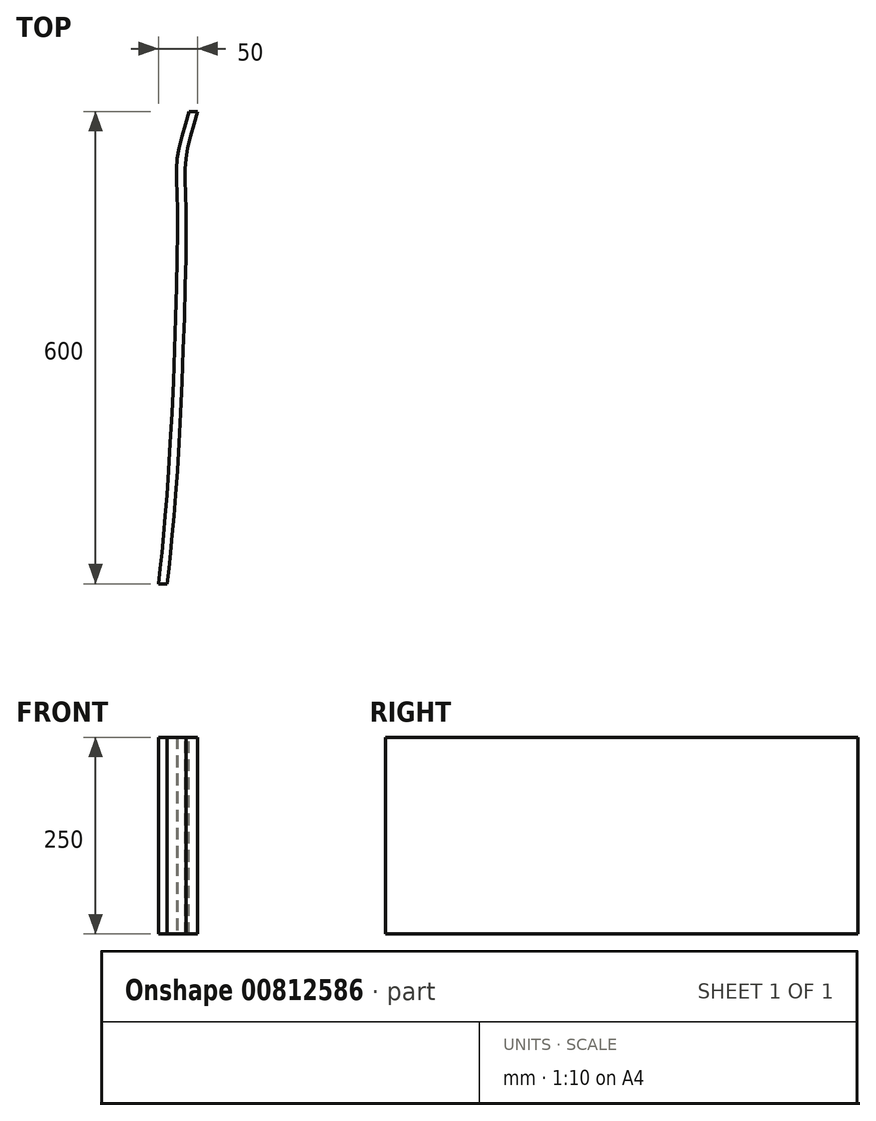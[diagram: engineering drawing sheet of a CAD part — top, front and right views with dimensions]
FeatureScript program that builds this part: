
annotation { "Feature Type Name" : "Feature", "Feature Type Description" : "" }
export const myFeature = defineFeature(function(context is Context, id is Id, definition is map)
    precondition{}
    {
        {
            var Q0;
            Q0=qCreatedBy(makeId("Front.planeOp"),FACE);
            var sketch = newSketch(context, id + "F0", { "sketchPlane" : qUnion([Q0])});
            skLineSegment(sketch, "E0", {"start": v(0, 0) * mm, "end": v(-800, 0) * mm});
            skLineSegment(sketch, "E1", {"start": v(0, 0) * mm, "end": v(800, 0) * mm});
            skPoint(sketch, "E2", {"position": v(800, 0) * mm});
            skSolve(sketch);
        }
        {
            var Q0;
            Q0=qCreatedBy(makeId("Right.planeOp"),FACE);
            cPlane(context, id + "F1", {"entities" : qUnion([Q0]), "cplaneType" : CPlaneType.OFFSET, "offset" : 800 * mm, "width" : 150 * mm, "height" : 150 * mm});
        }
        {
            var Q0;
            Q0=qCreatedBy(id+"F1.planeOp",FACE);
            var sketch = newSketch(context, id + "F2", { "sketchPlane" : qUnion([Q0])});
            skLineSegment(sketch, "E3", {"start": v(0, 0) * mm, "end": v(600, 0) * mm});
            skLineSegment(sketch, "E4", {"start": v(0, 0) * mm, "end": v(0, 250) * mm});
            skSolve(sketch);
        }
        {
            var Q0;
            Q0=sQuery(id+"F2.wireOp",EDGE,"E4");
            cPlane(context, id + "F3", {"entities" : qUnion([Q0]), "cplaneType" : CPlaneType.LINE_ANGLE, "offset" : 25 * mm, "angle" : 90 * degree, "oppositeDirection" : true, "width" : 150 * mm, "height" : 150 * mm});
        }
        {
            var Q0;
            Q0=qCreatedBy(id+"F3.planeOp",FACE);
            var sketch = newSketch(context, id + "F4", { "sketchPlane" : qUnion([Q0])});
            skLineSegment(sketch, "E5", {"start": v(0, 0) * mm, "end": v(800, 0) * mm});
            skLineSegment(sketch, "E6", {"start": v(800, 0) * mm, "end": v(750, 0) * mm});
            skLineSegment(sketch, "E7", {"start": v(750, 0) * mm, "end": v(750, 250) * mm});
            skLineSegment(sketch, "E8", {"start": v(750, 250) * mm, "end": v(761, 250) * mm});
            skLineSegment(sketch, "E9", {"start": v(761, 250) * mm, "end": v(761, 0) * mm});
            skSolve(sketch);
        }
        {
            var Q0;
            Q0=sQuery(id+"F0.wireOp",EDGE,"E1");
            cPlane(context, id + "F5", {"entities" : qUnion([Q0]), "cplaneType" : CPlaneType.LINE_ANGLE, "offset" : 25 * mm, "angle" : 90 * degree, "width" : 150 * mm, "height" : 150 * mm});
        }
        {
            var Q0;
            Q0=qCreatedBy(id+"F5.planeOp",FACE);
            var sketch = newSketch(context, id + "F6", { "sketchPlane" : qUnion([Q0])});
            skLineSegment(sketch, "E10", {"start": v(362.7, -706.38) * mm, "end": v(362.7, -1306.38) * mm});
            skLineSegment(sketch, "E11", {"start": v(362.7, -1306.38) * mm, "end": v(401.7, -1306.38) * mm});
            skFitSpline(sketch, "E12", {"points": [v(362.7, -706.38) * mm, v(370.44, -821.22) * mm, v(376.31, -1186.5) * mm, v(401.7, -1306.38) * mm], "startDerivative": vector(38, -347.66) * mm, "endDerivative": vector(111.55, -351.45) * mm});
            skLineSegment(sketch, "E13", {"start": v(-452.25, 1511.78) * mm, "end": v(-452.25, 911.78) * mm});
            skLineSegment(sketch, "E14", {"start": v(-452.25, 1511.78) * mm, "end": v(-413.25, 1511.78) * mm});
            skFitSpline(sketch, "E15", {"points": [v(-452.25, 911.78) * mm, v(-439.29, 1055.15) * mm, v(-428.15, 1387.9) * mm, v(-428.2, 1453.28) * mm, v(-413.25, 1511.78) * mm], "startDerivative": vector(50.52, 449.36) * mm, "endDerivative": vector(112.54, 364.86) * mm});
            skSolve(sketch);
        }
        {
            var Q0;
            {var subQ0=sQuery(id+"F4.wireOp",EDGE,"E7");Q0=makeQuery(id+"F4.imprint","IMPRINT",FACE,{"disambiguationData":[TD([[makeQuery(id+"F4.imprint","IMPRINT",EDGE,{"derivedFrom":subQ0}),-1.0]])]});}
            var Q1;
            Q1=sQuery(id+"F6.wireOp",EDGE,"E15");
            sweep(context, id + "F7", {"profiles" : qUnion([Q0]), "path" : qUnion([Q1]), "keepProfileOrientation" : true});
        }
        {
            var Q0;
            Q0=makeQuery(id+"F7.opSweep","CAP_EDGE",EDGE,{"disambiguationData":[OSD([sQuery(id+"F4.wireOp",EDGE,"E7"),sQuery(id+"F6.wireOp",VERTEX,"E15.start")])],"isStart":true});
            cPlane(context, id + "F8", {"entities" : qUnion([Q0]), "cplaneType" : CPlaneType.LINE_ANGLE, "offset" : 25 * mm, "angle" : 0 * degree, "width" : 150 * mm, "height" : 150 * mm});
        }
    });
